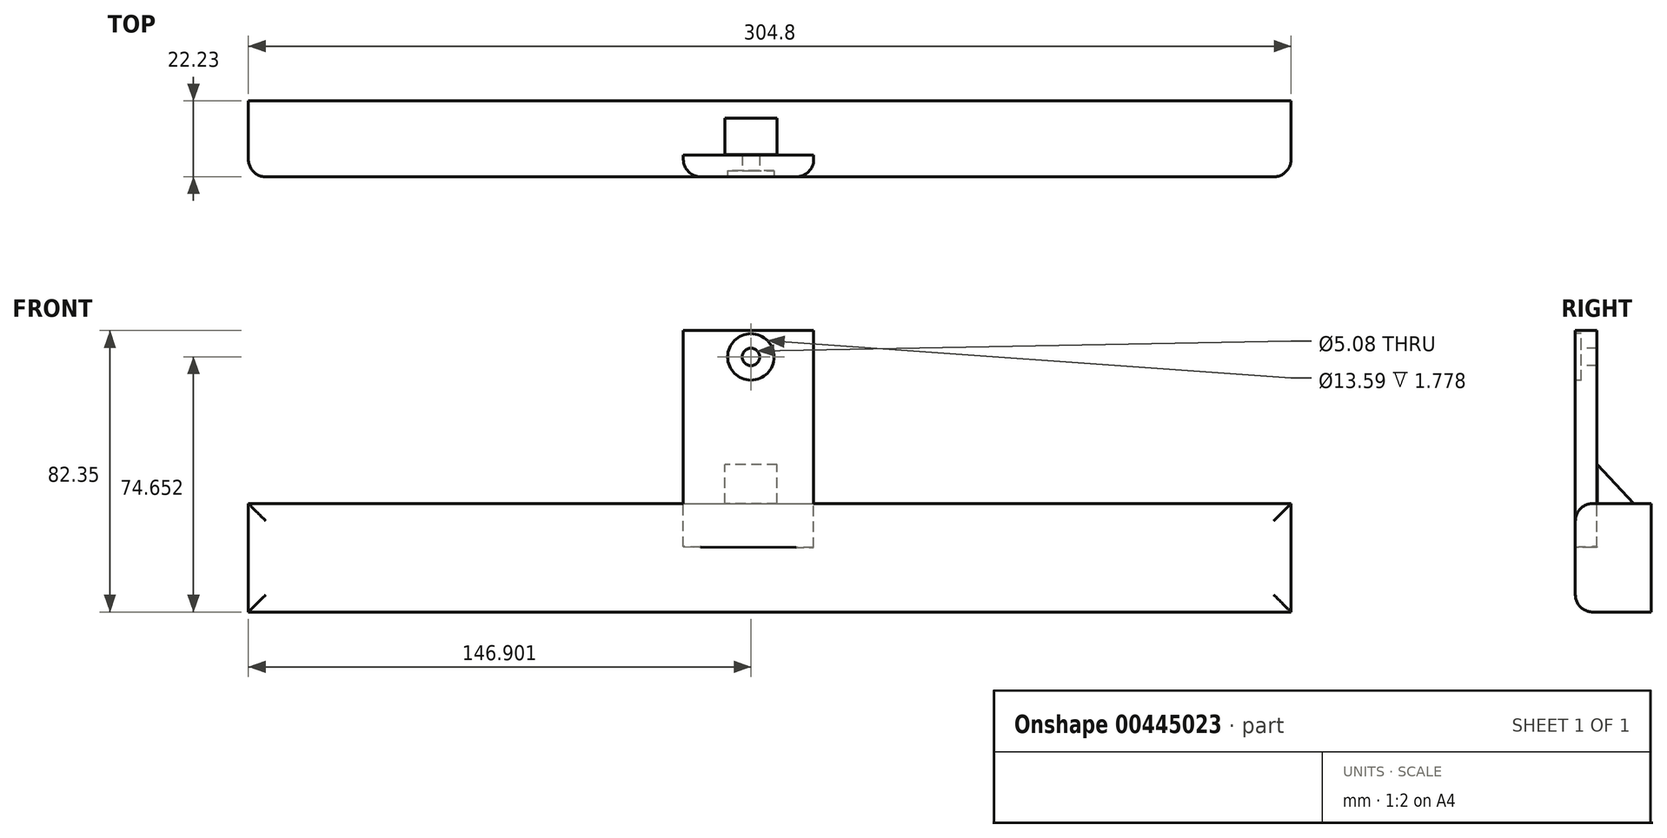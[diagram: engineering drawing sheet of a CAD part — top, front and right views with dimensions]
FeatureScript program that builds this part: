
annotation { "Feature Type Name" : "Feature", "Feature Type Description" : "" }
export const myFeature = defineFeature(function(context is Context, id is Id, definition is map)
    precondition{}
    {
        {
            var Q0;
            Q0=qCreatedBy(makeId("Front.planeOp"),FACE);
            var sketch = newSketch(context, id + "F0", { "sketchPlane" : qUnion([Q0])});
            skLineSegment(sketch, "E0.bottom", {"start": v(-154.58, 17.2) * mm, "end": v(150.22, 17.2) * mm});
            skLineSegment(sketch, "E0.top", {"start": v(-154.58, -14.55) * mm, "end": v(150.22, -14.55) * mm});
            skLineSegment(sketch, "E0.left", {"start": v(-154.58, 17.2) * mm, "end": v(-154.58, -14.55) * mm});
            skLineSegment(sketch, "E0.right", {"start": v(150.22, 17.2) * mm, "end": v(150.22, -14.55) * mm});
            skSolve(sketch);
        }
        {
            var Q0;
            Q0=makeQuery(id+"F0.imprint","IMPRINT",FACE,{"disambiguationData":[TD([[makeQuery(id+"F0.imprint","IMPRINT",EDGE,{"derivedFrom":sQuery(id+"F0.wireOp",EDGE,"E0.bottom")}),-1.0]])]});
            extrude(context, id + "F1", {"entities" : qUnion([Q0]), "oppositeDirection" : true, "depth" : 22.22 * mm});
        }
        {
            var Q0;
            Q0=qCreatedBy(makeId("Front.planeOp"),FACE);
            var sketch = newSketch(context, id + "F2", { "sketchPlane" : qUnion([Q0])});
            skLineSegment(sketch, "E1", {"start": v(-154.43, 17.25) * mm, "end": v(-27.43, 17.25) * mm, "construction": true});
            skLineSegment(sketch, "E2.top", {"start": v(-27.43, 67.8) * mm, "end": v(10.67, 67.8) * mm});
            skLineSegment(sketch, "E2.left", {"start": v(-27.43, 4.55) * mm, "end": v(-27.43, 67.8) * mm});
            skLineSegment(sketch, "E2.right", {"start": v(10.67, 4.3) * mm, "end": v(10.67, 67.8) * mm});
            skLineSegment(sketch, "E3", {"start": v(-27.43, 17.25) * mm, "end": v(-27.43, 4.55) * mm, "construction": true});
            skLineSegment(sketch, "E4", {"start": v(-27.43, 4.55) * mm, "end": v(10.67, 4.3) * mm});
            skSolve(sketch);
        }
        {
            var Q0;
            Q0=makeQuery(id+"F2.imprint","IMPRINT",FACE,{"disambiguationData":[TD([[makeQuery(id+"F2.imprint","IMPRINT",EDGE,{"derivedFrom":sQuery(id+"F2.wireOp",EDGE,"E2.top")}),-1.0]])]});
            extrude(context, id + "F3", {"entities" : qUnion([Q0]), "oppositeDirection" : true, "depth" : 6.35 * mm});
        }
        {
            var Q0;
            Q0=qCreatedBy(makeId("Front.planeOp"),FACE);
            var sketch = newSketch(context, id + "F4", { "sketchPlane" : qUnion([Q0])});
            skCircle(sketch, "E5", {"center": v(-7.68, 60.1) * mm, "radius": 2.54 * mm});
            skCircle(sketch, "E6", {"center": v(-7.68, 60.1) * mm, "radius": 6.8 * mm});
            skSolve(sketch);
        }
        {
            var Q0;
            Q0=makeQuery(id+"F4.imprint","IMPRINT",FACE,{"disambiguationData":[TD([[makeQuery(id+"F4.imprint","IMPRINT",EDGE,{"derivedFrom":sQuery(id+"F4.wireOp",EDGE,"E5")}),1.0]])]});
            var Q1;
            Q1=sQuery(id+"F4.wireOp",EDGE,"E5");
            extrude(context, id + "F5", {"entities" : qUnion([Q0]), "operationType" : NewBodyOperationType.REMOVE, "surfaceEntities" : qUnion([Q1]), "oppositeDirection" : true, "depth" : 25.4 * mm});
        }
        {
            var Q0;
            Q0 = qSketchRegion(id + "F4", true);
            extrude(context, id + "F6", {"entities" : qUnion([Q0]), "operationType" : NewBodyOperationType.REMOVE, "oppositeDirection" : true, "depth" : 1.78 * mm});
        }
        {
            var Q0;
            Q0=qCreatedBy(makeId("Right.planeOp"),FACE);
            cPlane(context, id + "F7", {"entities" : qUnion([Q0]), "cplaneType" : CPlaneType.OFFSET, "offset" : 15.24 * mm, "oppositeDirection" : true, "width" : 152.4 * mm, "height" : 152.4 * mm});
        }
        {
            var Q0;
            Q0=qCreatedBy(id+"F7.planeOp",FACE);
            var sketch = newSketch(context, id + "F8", { "sketchPlane" : qUnion([Q0])});
            skLineSegment(sketch, "E7", {"start": v(6.44, 28.55) * mm, "end": v(6.44, 17.16) * mm});
            skLineSegment(sketch, "E8", {"start": v(6.44, 17.16) * mm, "end": v(17.16, 17.16) * mm});
            skLineSegment(sketch, "E9", {"start": v(17.16, 17.16) * mm, "end": v(6.44, 28.55) * mm});
            skSolve(sketch);
        }
        {
            var Q0;
            Q0=makeQuery(id+"F8.imprint","IMPRINT",FACE,{"disambiguationData":[TD([[makeQuery(id+"F8.imprint","IMPRINT",EDGE,{"derivedFrom":sQuery(id+"F8.wireOp",EDGE,"E7")}),1.0]])]});
            extrude(context, id + "F9", {"entities" : qUnion([Q0]), "operationType" : NewBodyOperationType.ADD, "depth" : 15.24 * mm});
        }
        {
            var Q0;
            Q0=makeQuery(id+"F3.opExtrude","CAP_EDGE",EDGE,{"disambiguationData":[OSD([sQuery(id+"F2.wireOp",EDGE,"E2.right")])],"isStart":true});
            var Q1;
            Q1=makeQuery(id+"F3.opExtrude","CAP_EDGE",EDGE,{"disambiguationData":[OSD([sQuery(id+"F2.wireOp",EDGE,"E2.left")])],"isStart":true});
            var Q2;
            Q2=makeQuery(id+"F1.opExtrude","CAP_EDGE",EDGE,{"disambiguationData":[OSD([sQuery(id+"F0.wireOp",EDGE,"E0.top")])],"isStart":true});
            var Q3;
            Q3=makeQuery(id+"F1.opExtrude","CAP_EDGE",EDGE,{"disambiguationData":[OSD([sQuery(id+"F0.wireOp",EDGE,"E0.bottom")])],"isStart":true});
            var Q4;
            Q4=makeQuery(id+"F1.opExtrude","CAP_EDGE",EDGE,{"disambiguationData":[OSD([sQuery(id+"F0.wireOp",EDGE,"E0.right")])],"isStart":true});
            var Q5;
            Q5=makeQuery(id+"F1.opExtrude","CAP_EDGE",EDGE,{"disambiguationData":[OSD([sQuery(id+"F0.wireOp",EDGE,"E0.left")])],"isStart":true});
            fillet(context, id + "F10", {"entities" : qUnion([Q0, Q1, Q2, Q3, Q4, Q5]), "radius" : 5.08 * mm, "tangentPropagation" : true, "allowEdgeOverflow" : false});
        }
    });
